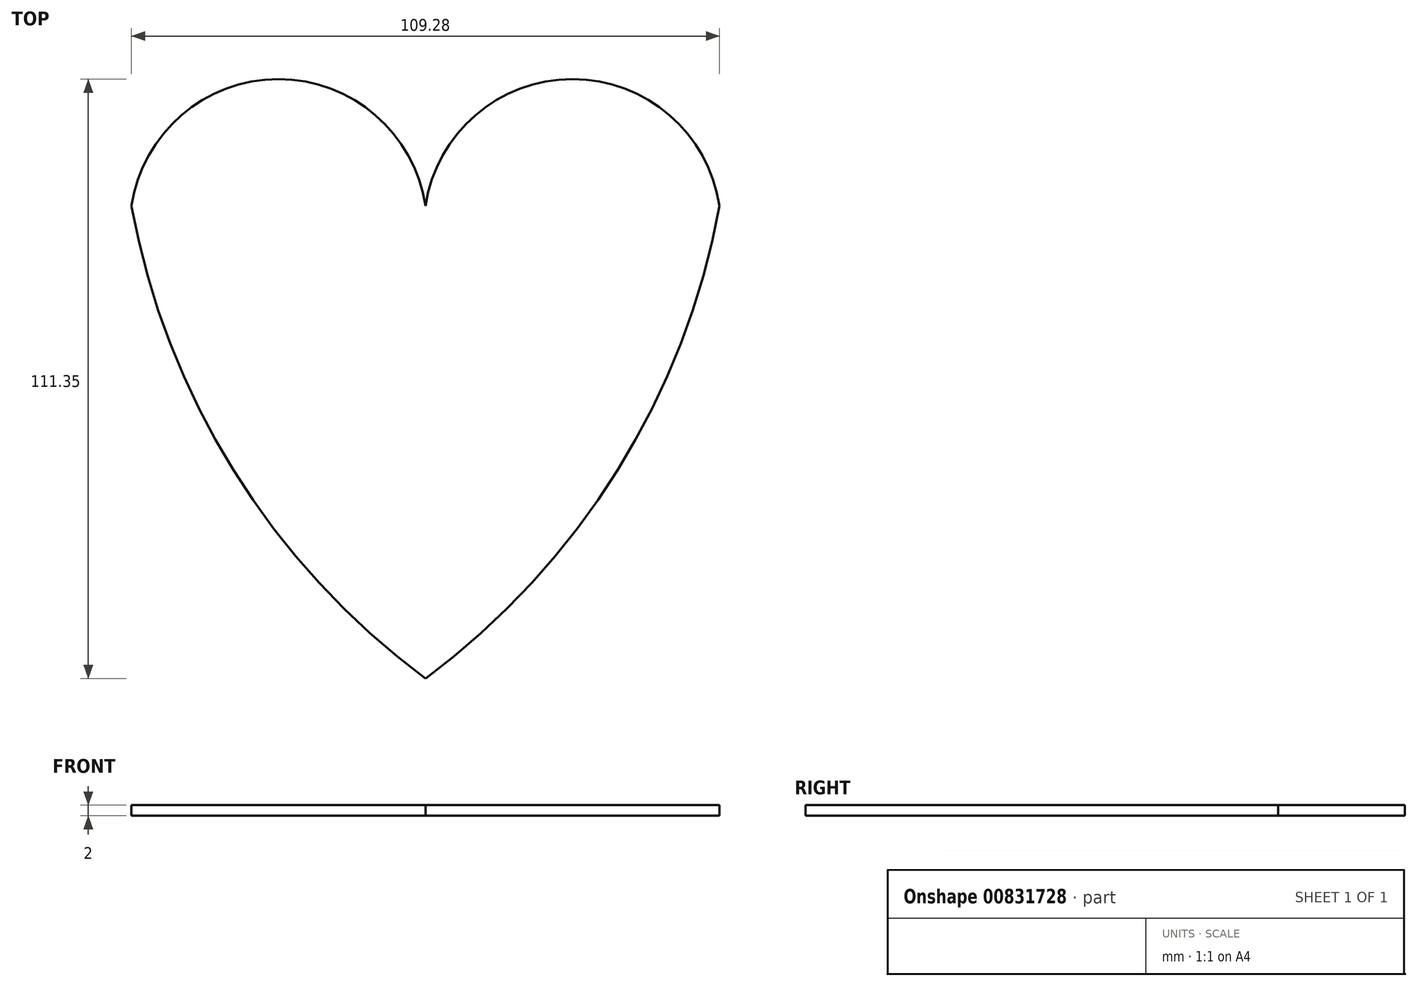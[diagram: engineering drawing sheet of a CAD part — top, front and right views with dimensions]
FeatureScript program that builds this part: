
annotation { "Feature Type Name" : "Feature", "Feature Type Description" : "" }
export const myFeature = defineFeature(function(context is Context, id is Id, definition is map)
    precondition{}
    {
        {
            var Q0;
            Q0=qCreatedBy(makeId("Top.planeOp"),FACE);
            var sketch = newSketch(context, id + "F0", { "sketchPlane" : qUnion([Q0])});
            skLineSegment(sketch, "E0", {"start": v(0, 74.5) * mm, "end": v(0, -74.5) * mm});
            skArc(sketch, "E1", {"start": v(-54.64, 28.6) * mm, "mid": v(-35.68, -20.5) * mm, "end": v(0, -59.2) * mm});
            skArc(sketch, "E2", {"start": v(0, 28.6) * mm, "mid": v(-27.32, 52.15) * mm, "end": v(-54.64, 28.6) * mm});
            skArc(sketch, "E3.MirrorCS", {"start": v(0, 28.6) * mm, "mid": v(27.32, 52.15) * mm, "end": v(54.64, 28.6) * mm});
            skArc(sketch, "E4.MirrorCS", {"start": v(54.64, 28.6) * mm, "mid": v(35.68, -20.5) * mm, "end": v(0, -59.2) * mm});
            skSolve(sketch);
        }
        {
            var Q0;
            Q0 = qSketchRegion(id + "F0", true);
            extrude(context, id + "F1", {"entities" : qUnion([Q0]), "depth" : 2 * mm, "offsetDistance" : 25 * mm});
        }
    });
